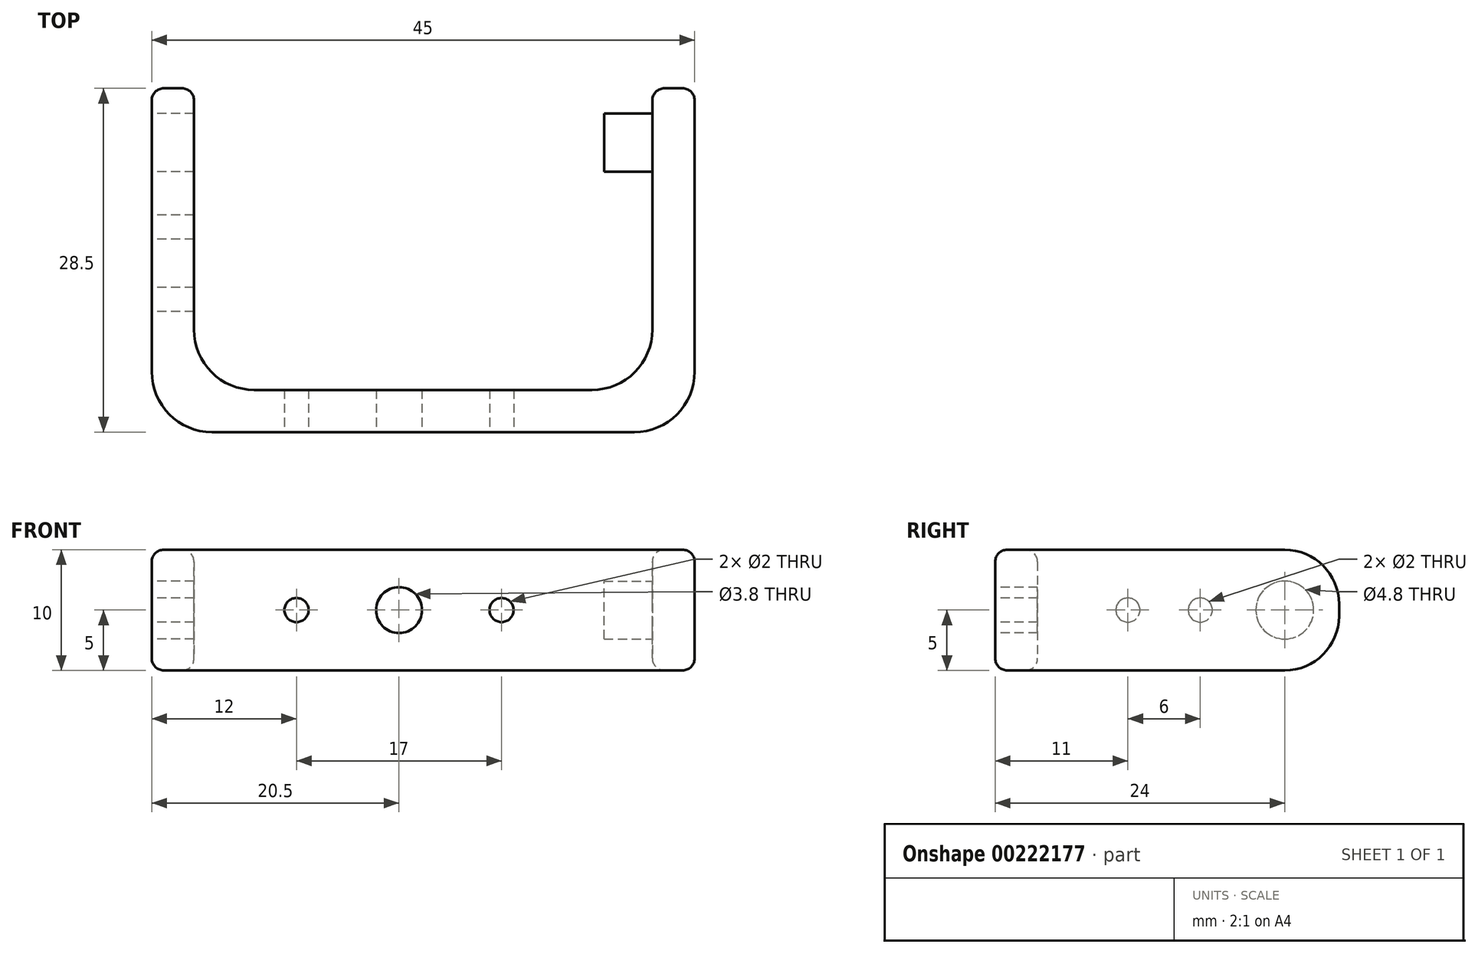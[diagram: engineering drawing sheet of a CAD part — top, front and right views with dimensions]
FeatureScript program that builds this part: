
annotation { "Feature Type Name" : "Feature", "Feature Type Description" : "" }
export const myFeature = defineFeature(function(context is Context, id is Id, definition is map)
    precondition{}
    {
        {
            var Q0;
            Q0=qCreatedBy(makeId("Top.planeOp"),FACE);
            var sketch = newSketch(context, id + "F0", { "sketchPlane" : qUnion([Q0])});
            skLineSegment(sketch, "E0", {"start": v(0, 0) * mm, "end": v(22.5, 0) * mm});
            skLineSegment(sketch, "E1", {"start": v(22.5, 0) * mm, "end": v(22.5, 28.5) * mm});
            skLineSegment(sketch, "E2", {"start": v(22.5, 28.5) * mm, "end": v(19, 28.5) * mm});
            skLineSegment(sketch, "E3", {"start": v(19, 28.5) * mm, "end": v(19, 3.5) * mm});
            skLineSegment(sketch, "E4", {"start": v(19, 3.5) * mm, "end": v(0, 3.5) * mm});
            skLineSegment(sketch, "E5.MirrorCS", {"start": v(-19, 3.5) * mm, "end": v(0, 3.5) * mm});
            skLineSegment(sketch, "E6.MirrorCS", {"start": v(-19, 28.5) * mm, "end": v(-19, 3.5) * mm});
            skLineSegment(sketch, "E7.MirrorCS", {"start": v(-22.5, 28.5) * mm, "end": v(-19, 28.5) * mm});
            skLineSegment(sketch, "E8.MirrorCS", {"start": v(-22.5, 0) * mm, "end": v(-22.5, 28.5) * mm});
            skLineSegment(sketch, "E9.MirrorCS", {"start": v(0, 0) * mm, "end": v(-22.5, 0) * mm});
            skSolve(sketch);
        }
        {
            var Q0;
            Q0=makeQuery(id+"F0.imprint","IMPRINT",FACE,{"disambiguationData":[TD([[makeQuery(id+"F0.imprint","IMPRINT",EDGE,{"derivedFrom":sQuery(id+"F0.wireOp",EDGE,"E0")}),1.0]])]});
            extrude(context, id + "F1", {"entities" : qUnion([Q0]), "depth" : 10 * mm});
        }
        {
            var Q0;
            Q0=makeQuery(id+"F1.opExtrude","CAP_EDGE",EDGE,{"disambiguationData":[OSD([sQuery(id+"F0.wireOp",EDGE,"E7.MirrorCS")])],"isStart":false});
            var Q1;
            Q1=makeQuery(id+"F1.opExtrude","CAP_EDGE",EDGE,{"disambiguationData":[OSD([sQuery(id+"F0.wireOp",EDGE,"E7.MirrorCS")])],"isStart":true});
            var Q2;
            Q2=makeQuery(id+"F1.opExtrude","CAP_EDGE",EDGE,{"disambiguationData":[OSD([sQuery(id+"F0.wireOp",EDGE,"E2")])],"isStart":false});
            var Q3;
            Q3=makeQuery(id+"F1.opExtrude","CAP_EDGE",EDGE,{"disambiguationData":[OSD([sQuery(id+"F0.wireOp",EDGE,"E2")])],"isStart":true});
            fillet(context, id + "F2", {"entities" : qUnion([Q0, Q1, Q2, Q3]), "radius" : 4.5 * mm, "tangentPropagation" : true, "allowEdgeOverflow" : false});
        }
        {
            var Q0;
            Q0=makeQuery(id+"F1.opExtrude","SWEPT_FACE",FACE,{"disambiguationData":[OSD([sQuery(id+"F0.wireOp",EDGE,"E8.MirrorCS")])]});
            var sketch = newSketch(context, id + "F3", { "sketchPlane" : qUnion([Q0])});
            skLineSegment(sketch, "E10", {"start": v(1.5, 5) * mm, "end": v(-31.56, 5) * mm, "construction": true});
            skPoint(sketch, "E10.startSnap0", {"position": v(0, 5) * mm});
            skCircle(sketch, "E11", {"center": v(-24, 5) * mm, "radius": 2.4 * mm});
            skCircle(sketch, "E12", {"center": v(-17, 5) * mm, "radius": 1 * mm});
            skCircle(sketch, "E13", {"center": v(-11, 5) * mm, "radius": 1 * mm});
            skSolve(sketch);
        }
        {
            var Q0;
            Q0=makeQuery(id+"F3.imprint","IMPRINT",FACE,{"disambiguationData":[TD([[makeQuery(id+"F3.imprint","IMPRINT",EDGE,{"derivedFrom":sQuery(id+"F3.wireOp",EDGE,"E12")}),1.0]])]});
            var Q1;
            Q1=makeQuery(id+"F3.imprint","IMPRINT",FACE,{"disambiguationData":[TD([[makeQuery(id+"F3.imprint","IMPRINT",EDGE,{"derivedFrom":sQuery(id+"F3.wireOp",EDGE,"E13")}),1.0]])]});
            extrude(context, id + "F4", {"entities" : qUnion([Q0, Q1]), "operationType" : NewBodyOperationType.REMOVE, "oppositeDirection" : true, "depth" : 4 * mm});
        }
        {
            var Q0;
            Q0=makeQuery(id+"F1.opExtrude","SWEPT_FACE",FACE,{"disambiguationData":[OSD([sQuery(id+"F0.wireOp",EDGE,"E1")])]});
            var sketch = newSketch(context, id + "F5", { "sketchPlane" : qUnion([Q0])});
            skCircle(sketch, "E14", {"center": v(24, 5) * mm, "radius": 2.4 * mm});
            skSolve(sketch);
        }
        {
            var Q0;
            Q0=makeQuery(id+"F5.imprint","IMPRINT",FACE,{"disambiguationData":[TD([[makeQuery(id+"F5.imprint","IMPRINT",EDGE,{"derivedFrom":sQuery(id+"F5.wireOp",EDGE,"E14")}),1.0]])]});
            extrude(context, id + "F6", {"entities" : qUnion([Q0]), "operationType" : NewBodyOperationType.ADD, "oppositeDirection" : true, "depth" : 7.5 * mm});
        }
        {
            var Q0;
            Q0=makeQuery(id+"F3.imprint","IMPRINT",FACE,{"disambiguationData":[TD([[makeQuery(id+"F3.imprint","IMPRINT",EDGE,{"derivedFrom":sQuery(id+"F3.wireOp",EDGE,"E11")}),1.0]])]});
            extrude(context, id + "F7", {"entities" : qUnion([Q0]), "operationType" : NewBodyOperationType.REMOVE, "oppositeDirection" : true, "depth" : 25 * mm, "hasSecondDirection" : true, "secondDirectionOppositeDirection" : false, "secondDirectionDepth" : 25 * mm});
        }
        {
            var Q0;
            Q0=makeQuery(id+"F1.opExtrude","SWEPT_EDGE",EDGE,{"disambiguationData":[OSD([sQuery(id+"F0.wireOp",EDGE,"E8.MirrorCS"),sQuery(id+"F0.wireOp",EDGE,"E9.MirrorCS")])]});
            var Q1;
            Q1=makeQuery(id+"F1.opExtrude","SWEPT_EDGE",EDGE,{"disambiguationData":[OSD([sQuery(id+"F0.wireOp",EDGE,"E0"),sQuery(id+"F0.wireOp",EDGE,"E1")])]});
            var Q2;
            Q2=makeQuery(id+"F1.opExtrude","SWEPT_EDGE",EDGE,{"disambiguationData":[OSD([sQuery(id+"F0.wireOp",EDGE,"E5.MirrorCS"),sQuery(id+"F0.wireOp",EDGE,"E6.MirrorCS")])]});
            var Q3;
            Q3=makeQuery(id+"F1.opExtrude","SWEPT_EDGE",EDGE,{"disambiguationData":[OSD([sQuery(id+"F0.wireOp",EDGE,"E3"),sQuery(id+"F0.wireOp",EDGE,"E4")])]});
            fillet(context, id + "F8", {"entities" : qUnion([Q0, Q1, Q2, Q3]), "radius" : 5 * mm, "tangentPropagation" : true, "allowEdgeOverflow" : false});
        }
        {
            var Q0;
            Q0=makeQuery(id+"F1.opExtrude","SWEPT_FACE",FACE,{"disambiguationData":[OSD([sQuery(id+"F0.wireOp",EDGE,"E0"),sQuery(id+"F0.wireOp",EDGE,"E9.MirrorCS")])]});
            var sketch = newSketch(context, id + "F9", { "sketchPlane" : qUnion([Q0])});
            skLineSegment(sketch, "E15", {"start": v(-17.5, 5) * mm, "end": v(17.5, 5) * mm, "construction": true});
            skCircle(sketch, "E16", {"center": v(-2, 5) * mm, "radius": 1.9 * mm});
            skCircle(sketch, "E17", {"center": v(-10.5, 5) * mm, "radius": 1 * mm});
            skCircle(sketch, "E18", {"center": v(6.5, 5) * mm, "radius": 1 * mm});
            skSolve(sketch);
        }
        {
            var Q0;
            Q0=makeQuery(id+"F9.imprint","IMPRINT",FACE,{"disambiguationData":[TD([[makeQuery(id+"F9.imprint","IMPRINT",EDGE,{"derivedFrom":sQuery(id+"F9.wireOp",EDGE,"E17")}),1.0]])]});
            var Q1;
            Q1=makeQuery(id+"F9.imprint","IMPRINT",FACE,{"disambiguationData":[TD([[makeQuery(id+"F9.imprint","IMPRINT",EDGE,{"derivedFrom":sQuery(id+"F9.wireOp",EDGE,"E16")}),1.0]])]});
            var Q2;
            Q2=makeQuery(id+"F9.imprint","IMPRINT",FACE,{"disambiguationData":[TD([[makeQuery(id+"F9.imprint","IMPRINT",EDGE,{"derivedFrom":sQuery(id+"F9.wireOp",EDGE,"E18")}),1.0]])]});
            extrude(context, id + "F10", {"entities" : qUnion([Q0, Q1, Q2]), "operationType" : NewBodyOperationType.REMOVE, "oppositeDirection" : true, "depth" : 25 * mm, "hasSecondDirection" : true, "secondDirectionOppositeDirection" : false, "secondDirectionDepth" : 25 * mm});
        }
        {
            var Q0;
            Q0=makeQuery(id+"F1.opExtrude","CAP_FACE",FACE,{"disambiguationData":[OSD([sQuery(id+"F0.wireOp",EDGE,"E0"),sQuery(id+"F0.wireOp",EDGE,"E1"),sQuery(id+"F0.wireOp",EDGE,"E2"),sQuery(id+"F0.wireOp",EDGE,"E3"),sQuery(id+"F0.wireOp",EDGE,"E4"),sQuery(id+"F0.wireOp",EDGE,"E5.MirrorCS"),sQuery(id+"F0.wireOp",EDGE,"E6.MirrorCS"),sQuery(id+"F0.wireOp",EDGE,"E7.MirrorCS"),sQuery(id+"F0.wireOp",EDGE,"E8.MirrorCS"),sQuery(id+"F0.wireOp",EDGE,"E9.MirrorCS")])],"isStart":true});
            fillet(context, id + "F11", {"entities" : qUnion([Q0]), "radius" : 1 * mm, "tangentPropagation" : true, "allowEdgeOverflow" : false});
        }
    });
